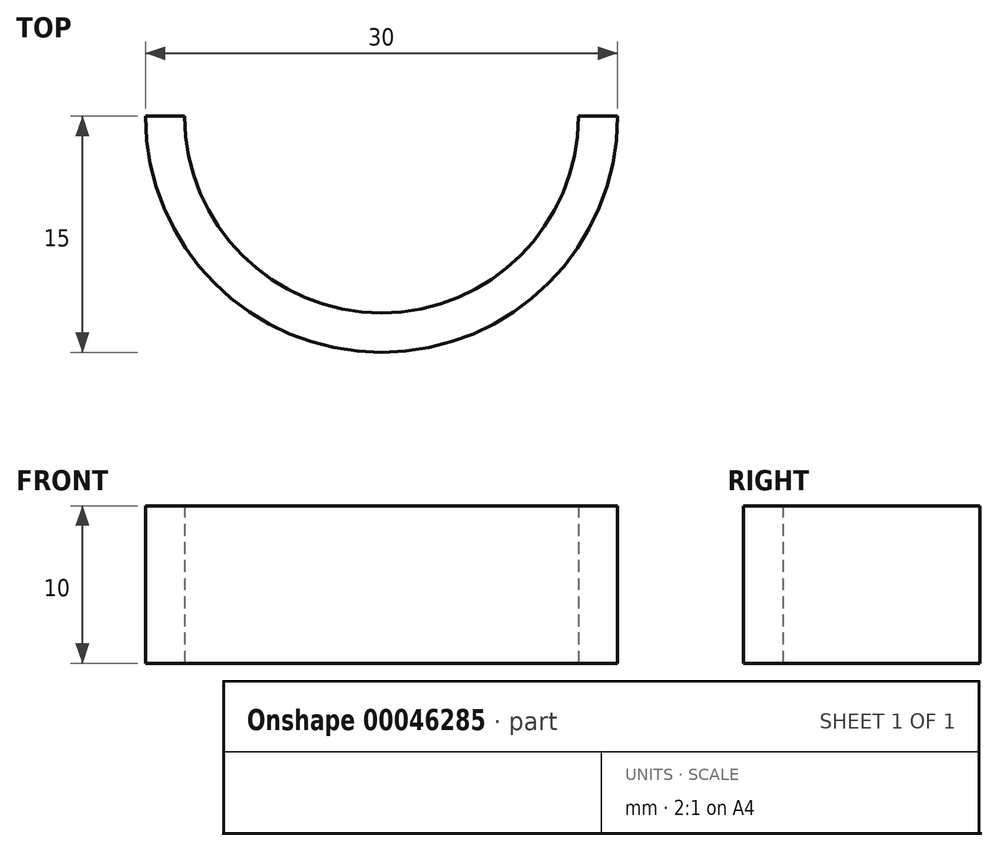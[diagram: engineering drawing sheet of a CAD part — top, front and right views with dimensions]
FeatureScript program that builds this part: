
annotation { "Feature Type Name" : "Feature", "Feature Type Description" : "" }
export const myFeature = defineFeature(function(context is Context, id is Id, definition is map)
    precondition{}
    {
        {
            var Q0;
            Q0=qCreatedBy(makeId("Top.planeOp"),FACE);
            var sketch = newSketch(context, id + "F0", { "sketchPlane" : qUnion([Q0])});
            skCircle(sketch, "E0", {"center": v(0, 0) * mm, "radius": 12.5 * mm});
            skCircle(sketch, "E1", {"center": v(0, 0) * mm, "radius": 15 * mm});
            skLineSegment(sketch, "E2", {"start": v(-15, 0) * mm, "end": v(-12.5, 0) * mm});
            skLineSegment(sketch, "E3", {"start": v(12.5, 0) * mm, "end": v(15, 0) * mm});
            skSolve(sketch);
        }
        {
            var Q0;
            {var subQ1=sQuery(id+"F0.wireOp",EDGE,"E2");Q0=makeQuery(id+"F0.imprint","IMPRINT",FACE,{"disambiguationData":[TD([[makeQuery(id+"F0.imprint","IMPRINT",EDGE,{"derivedFrom":subQ1}),-1.0]])]});}
            extrude(context, id + "F1", {"entities" : qUnion([Q0]), "depth" : 10 * mm});
        }
    });
